# Revit family: Tyco_Fire Detector_and_Alarm Control_Indicator_Equipment-Profile Flexible Housings
name_source: partatom
category: Fire Alarm Devices
revit_build: Autodesk Revit 2014 (Build: 20130308_1515(x64)
units: mm (PartAtom-declared; Revit-internal decimal feet)

## types (3) — shared parameters
Asset Type = Moveable
Brand = Zettler
Clearance = Yes
Colour = RAL 7016 (Anthracite Grey) & RAL 7040 (Window Grey)
Default Elevation = 1219 mm
Manufacturer = Tyco Fire Protection Products
Manufacturer URL = www.zettlerfire.com
Material = Mild steel Zintec (Electro Zinc Coated)
Nominal Height = 237 mm  [stored 0.777559 ft]
Nominal Length = 263 mm  [stored 0.862861 ft]
Nominal Width = 438 mm  [stored 1.43701 ft]
Operation Temperature Range = -8 °C to +55 °C
Relative Humidity = 90% RH continuous (non-condensing)
Shape = Rectangle
Storage Temperature = -20 °C to +70 °C
URL = http://www.zettlerfire.com
Warranty Duration Labor = 1.5
Warranty Duration Parts = 1.5
Warranty Duration Unit = Year
zero-valued in all types: Expected Life, Replacement Cost

## per-type parameters (varying)
| type | Description | Model | Model Number | Name | PXB800 | PX_AN/PR | Product Codes | Product Specification |
| PX-AN PROFILE | PX-AN PROFILE Aperture Expansion Housing for Annunciator Modules ANN840 ANN880 and  ANN820 | PX-AN | PX-AN | PX-AN PROFILE Aperture Expansion Housing for Annunciator Modules ANN840 ANN880 and  ANN820 | No | Yes | 557.202.863 | PX-AN PROFILE Aperture Expansion Housing for Annunciator Modules ANN840 ANN880 and  ANN820 |
| PXB800 PROFILE | PBB800 PROFILE Ancillary Expansion Box with mounting frame, door supports PZ4x or PZ8x | PXB800 | PXB800 | PBB800 PROFILE Ancillary Expansion Box with mounting frame, door supports PZ4x or PZ8x | Yes | No | 557.202.853 | PBB800 PROFILE Ancillary Expansion Box with mounting frame, door supports PZ4x or PZ8x |
| PX-PR PROFILE | PX-PR PROFILE 40 Column Thermal Printer in PXB800 Expansion Housing | PX-PR | PX-PR | PX-PR PROFILE 40 Column Thermal Printer in PXB800 Expansion Housing | No | Yes | 557.202.864 | PX-PR PROFILE 40 Column Thermal Printer in PXB800 Expansion Housing |

note: [stored X ft] marks values corroborated as IEEE doubles in the binary element streams (Revit-internal decimal feet)

## geometry (parser evidence)
native form markers: Sweep x7
no freeform markers — native parametric forms only
